# Revit family: Flush_Valve-Urinal_Concealed-American_Standard-Selectronic-Exposed_Back_Spud-606B3XX
name_source: partatom
category: Plumbing Fixtures
units: mm (PartAtom-declared; Revit-internal decimal feet)

## family parameters
Cut with Voids When Loaded = Yes
Host = Face
OmniClass Number = 23.65.70.00
OmniClass Title = Terminals for Supplied Liquids and Gases
Part Type = Normal
Room Calculation Point = No
Round Connector Dimension = Use Diameter
Shared = Yes

## types (3) — shared parameters
ADA Compliant = Yes
Activation = Hands-free Operation
Assembly Code = D2020100
CW Connection = Yes
CWFU = 5
CalGreen Compliant = Yes
Cold Water Connection Diameter = 3/4"
Compliance Certifications = ASSE 1037, ANSI/ASME A112.19.2
Default Elevation = 28"
Description = Ultima™ Selectronic Concealed Urinal Flush Valve, Base Model, Piston-Type, 0.125 gpf/0.5 Lpf
Distance from Valve to Suppy NPT (4 1/4" to 5 1/4") = 4 1/4"
Distance from Valve to Suppy NPT Constrain = 4 1/4"
Finish = Stainless Steel-American Standard-007-Chrome
Finish- Flush Valve = Brass-American Standard-Satin
Flow Requirement = 10 gpm/37.9 L/min
HW Connection = No
Installation Type = Exposed Back Spud
Manufacturer = American Standard
Material = Brass-American Standard-Satin
Operating Pressure = 20 psi (flowing) - 80 psi (static)
PK00.CRP CR-P2 Lithium Battery and Holder = No
PK00.HAC Hard-Wired AC Transformer, 10' Extension Cable and Single AC Adapter = No
PK00.MAC Multi-AC Adapter and 10" Extension Cable = No
PK00.PAC Plug-In AC Transformer and Single AC Adapter = No
PK00.WRK CR-P2 Lithium Battery and Holder = No
Price = Prices may vary. Please consult Manufacturer Representative for most up-to-date price list.
Product Documentation Link = https://americanstandard.box.com
Product Page URL = https://www.americanstandard-us.com
Revised Date = 11/17/2022
Top of Spud to Fixture Connection = 14"
Top of Spud to Fixture Connection Constrain = 14"
URL = http://www.americanstandard-us.com
Valve Distance from Wall (max. 8") = 8"
Valve Distance from Wall Constrain = 8"
Vent Connection = No
WFU = 5
Waste Connection = No
zero-valued in all types: HWFU

## per-type parameters (varying)
| type | EPA WaterSense® Certified | Flush Rate |
| 606B301.007 | Yes | 0.125 gpf/0.5 Lpf |
| 606B305.007 | Yes | 0.5 gpf/1.9 Lpf |
| 606B310.007 | No | 1.0 gpf/3.8 Lpf |

note: column(s) folded — value = type name in every type: Model

## geometry (parser evidence)
native form markers: Sweep x2
no freeform markers — native parametric forms only
